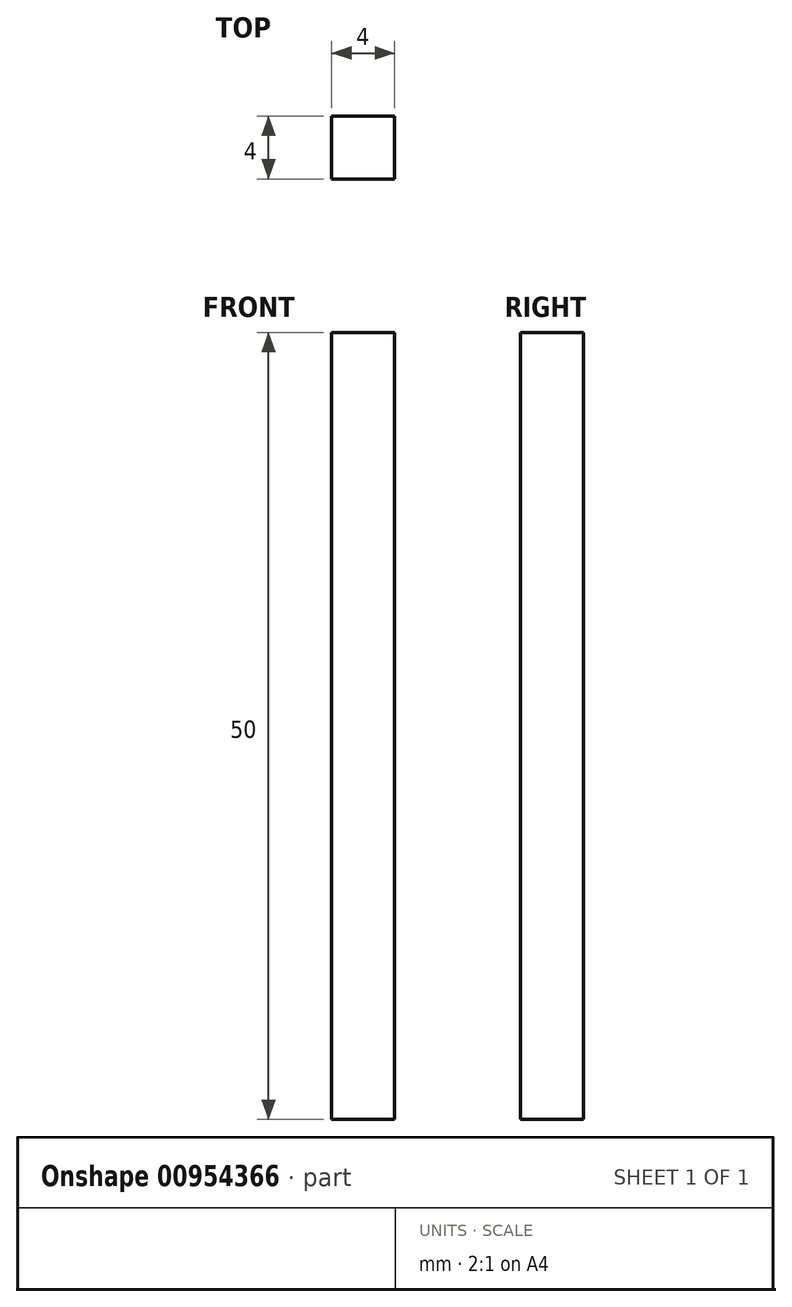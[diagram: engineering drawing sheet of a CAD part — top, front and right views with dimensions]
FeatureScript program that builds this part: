
annotation { "Feature Type Name" : "Feature", "Feature Type Description" : "" }
export const myFeature = defineFeature(function(context is Context, id is Id, definition is map)
    precondition{}
    {
        {
            var Q0;
            Q0=qCreatedBy(makeId("Top.planeOp"),FACE);
            var sketch = newSketch(context, id + "F0", { "sketchPlane" : qUnion([Q0])});
            skLineSegment(sketch, "E0.bottom", {"start": v(2, -2) * mm, "end": v(-2, -2) * mm});
            skLineSegment(sketch, "E0.top", {"start": v(2, 2) * mm, "end": v(-2, 2) * mm});
            skLineSegment(sketch, "E0.left", {"start": v(2, -2) * mm, "end": v(2, 2) * mm});
            skLineSegment(sketch, "E0.right", {"start": v(-2, -2) * mm, "end": v(-2, 2) * mm});
            skPoint(sketch, "E0.middle", {"position": v(0, 0) * mm});
            skSolve(sketch);
        }
        {
            var Q0;
            Q0=makeQuery(id+"F0.imprint","IMPRINT",FACE,{"disambiguationData":[TD([[makeQuery(id+"F0.imprint","IMPRINT",EDGE,{"derivedFrom":sQuery(id+"F0.wireOp",EDGE,"E0.bottom")}),-1.0]])]});
            extrude(context, id + "F1", {"entities" : qUnion([Q0]), "endBound" : BoundingType.SYMMETRIC, "depth" : 50 * mm, "offsetDistance" : 25 * mm});
        }
    });
